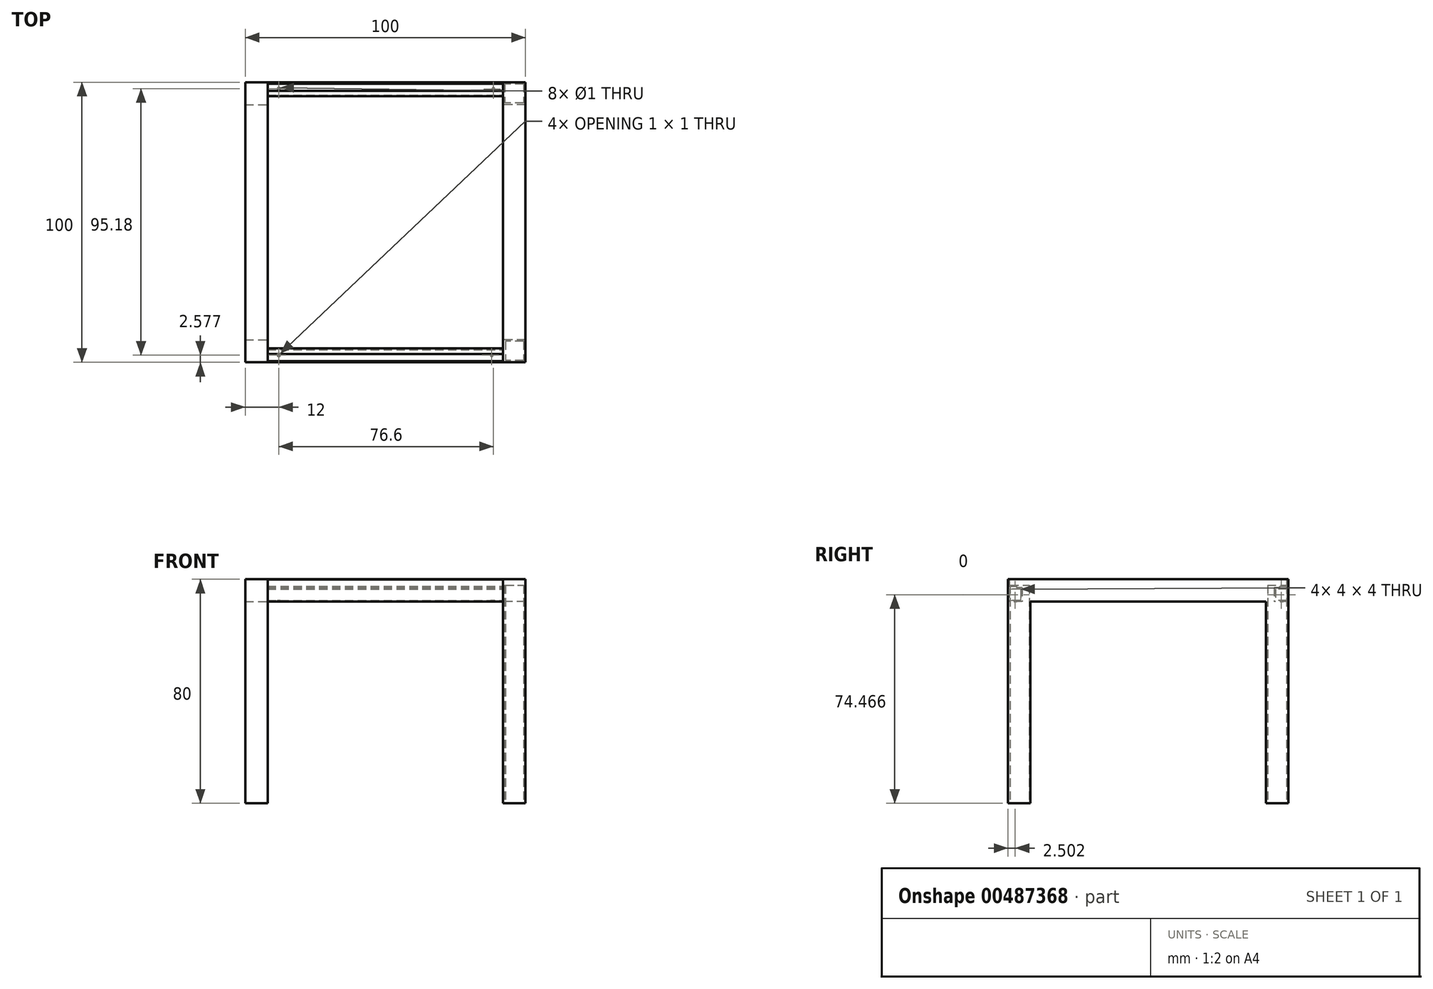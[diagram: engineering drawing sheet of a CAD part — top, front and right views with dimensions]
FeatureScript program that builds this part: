
annotation { "Feature Type Name" : "Feature", "Feature Type Description" : "" }
export const myFeature = defineFeature(function(context is Context, id is Id, definition is map)
    precondition{}
    {
        {
            var Q0;
            Q0=qCreatedBy(makeId("Right.planeOp"),FACE);
            var sketch = newSketch(context, id + "F0", { "sketchPlane" : qUnion([Q0])});
            skLineSegment(sketch, "E0", {"start": v(-60.79, -34.5) * mm, "end": v(-52.79, -34.5) * mm});
            skLineSegment(sketch, "E1", {"start": v(-52.79, -34.5) * mm, "end": v(-52.79, 37.5) * mm});
            skLineSegment(sketch, "E2", {"start": v(-52.79, 37.5) * mm, "end": v(31.21, 37.5) * mm});
            skLineSegment(sketch, "E3", {"start": v(31.21, 37.5) * mm, "end": v(31.21, -34.5) * mm});
            skLineSegment(sketch, "E4", {"start": v(31.21, -34.5) * mm, "end": v(39.21, -34.5) * mm});
            skLineSegment(sketch, "E5", {"start": v(39.21, -34.5) * mm, "end": v(39.21, 45.5) * mm});
            skLineSegment(sketch, "E6", {"start": v(39.21, 45.5) * mm, "end": v(-60.79, 45.5) * mm});
            skLineSegment(sketch, "E7", {"start": v(-60.79, 45.5) * mm, "end": v(-60.79, -34.5) * mm});
            skSolve(sketch);
        }
        {
            var Q0;
            Q0 = qSketchRegion(id + "F0", true);
            extrude(context, id + "F1", {"entities" : qUnion([Q0]), "depth" : 8 * mm});
        }
        {
            var Q0;
            Q0=qCreatedBy(makeId("Top.planeOp"),FACE);
            var sketch = newSketch(context, id + "F2", { "sketchPlane" : qUnion([Q0])});
            skLineSegment(sketch, "E8.bottom", {"start": v(0.9, -60.09) * mm, "end": v(7.35, -60.09) * mm});
            skLineSegment(sketch, "E8.top", {"start": v(0.9, -53.29) * mm, "end": v(7.35, -53.29) * mm});
            skLineSegment(sketch, "E8.left", {"start": v(0.9, -60.09) * mm, "end": v(0.9, -53.29) * mm});
            skLineSegment(sketch, "E8.right", {"start": v(7.35, -60.09) * mm, "end": v(7.35, -53.29) * mm});
            skLineSegment(sketch, "E9.bottom", {"start": v(0.6, 31.81) * mm, "end": v(7.35, 31.81) * mm});
            skLineSegment(sketch, "E9.top", {"start": v(0.6, 38.61) * mm, "end": v(7.35, 38.61) * mm});
            skLineSegment(sketch, "E9.left", {"start": v(0.6, 31.81) * mm, "end": v(0.6, 38.61) * mm});
            skLineSegment(sketch, "E9.right", {"start": v(7.35, 31.81) * mm, "end": v(7.35, 38.61) * mm});
            skSolve(sketch);
        }
        {
            var Q0;
            Q0 = qSketchRegion(id + "F2", true);
            extrude(context, id + "F3", {"entities" : qUnion([Q0]), "operationType" : NewBodyOperationType.REMOVE, "endBound" : BoundingType.SYMMETRIC, "depth" : 86.8 * mm});
        }
        {
            var Q0;
            Q0=qCreatedBy(makeId("Right.planeOp"),FACE);
            var sketch = newSketch(context, id + "F4", { "sketchPlane" : qUnion([Q0])});
            skLineSegment(sketch, "E10.bottom", {"start": v(39.2, 42.5) * mm, "end": v(34.2, 42.5) * mm});
            skLineSegment(sketch, "E10.top", {"start": v(39.2, 37.5) * mm, "end": v(34.2, 37.5) * mm});
            skLineSegment(sketch, "E10.left", {"start": v(39.2, 42.5) * mm, "end": v(39.2, 37.5) * mm});
            skLineSegment(sketch, "E10.right", {"start": v(34.2, 42.5) * mm, "end": v(34.2, 37.5) * mm});
            skLineSegment(sketch, "E11", {"start": v(39.21, 45.5) * mm, "end": v(39.2, 42.5) * mm});
            skLineSegment(sketch, "E12", {"start": v(36.2, 42.5) * mm, "end": v(36.2, 43) * mm});
            skLineSegment(sketch, "E13", {"start": v(36.2, 43) * mm, "end": v(38.71, 43) * mm});
            skLineSegment(sketch, "E14", {"start": v(38.71, 43) * mm, "end": v(38.71, 45.5) * mm});
            skLineSegment(sketch, "E15", {"start": v(38.71, 45.5) * mm, "end": v(39.21, 45.5) * mm});
            skLineSegment(sketch, "E16.bottom", {"start": v(38.7, 42) * mm, "end": v(34.7, 42) * mm});
            skLineSegment(sketch, "E16.top", {"start": v(38.7, 38) * mm, "end": v(34.7, 38) * mm});
            skLineSegment(sketch, "E16.left", {"start": v(38.7, 42) * mm, "end": v(38.7, 38) * mm});
            skLineSegment(sketch, "E16.right", {"start": v(34.7, 42) * mm, "end": v(34.7, 38) * mm});
            skLineSegment(sketch, "E17.bottom", {"start": v(-55.79, 42.5) * mm, "end": v(-60.79, 42.5) * mm});
            skLineSegment(sketch, "E17.top", {"start": v(-55.79, 37.5) * mm, "end": v(-60.79, 37.5) * mm});
            skLineSegment(sketch, "E17.left", {"start": v(-55.79, 42.5) * mm, "end": v(-55.79, 37.5) * mm});
            skLineSegment(sketch, "E17.right", {"start": v(-60.79, 42.5) * mm, "end": v(-60.79, 37.5) * mm});
            skLineSegment(sketch, "E18", {"start": v(-60.79, 45.5) * mm, "end": v(-60.29, 45.5) * mm});
            skLineSegment(sketch, "E19", {"start": v(-60.29, 45.5) * mm, "end": v(-60.29, 43) * mm});
            skLineSegment(sketch, "E20", {"start": v(-60.29, 43) * mm, "end": v(-57.79, 43) * mm});
            skLineSegment(sketch, "E21", {"start": v(-57.79, 43) * mm, "end": v(-57.79, 42.5) * mm});
            skLineSegment(sketch, "E22", {"start": v(-60.79, 45.5) * mm, "end": v(-60.79, 42.5) * mm});
            skLineSegment(sketch, "E23.bottom", {"start": v(-56.29, 41.98) * mm, "end": v(-60.29, 41.98) * mm});
            skLineSegment(sketch, "E23.top", {"start": v(-56.29, 37.98) * mm, "end": v(-60.29, 37.98) * mm});
            skLineSegment(sketch, "E23.left", {"start": v(-56.29, 41.98) * mm, "end": v(-56.29, 37.98) * mm});
            skLineSegment(sketch, "E23.right", {"start": v(-60.29, 41.98) * mm, "end": v(-60.29, 37.98) * mm});
            skLineSegment(sketch, "E24", {"start": v(-57.79, 42.5) * mm, "end": v(-60.79, 42.5) * mm});
            skSolve(sketch);
        }
        {
            var Q0;
            Q0 = qSketchRegion(id + "F4", true);
            extrude(context, id + "F5", {"entities" : qUnion([Q0]), "oppositeDirection" : true, "depth" : 84 * mm});
        }
        {
            var Q0;
            Q0 = qSketchRegion(id + "F4", true);
            extrude(context, id + "F6", {"entities" : qUnion([Q0]), "oppositeDirection" : true, "depth" : 84 * mm});
        }
        {
            var Q0;
            Q0=makeQuery(id+"F1.opExtrude","CAP_FACE",FACE,{"disambiguationData":[OSD([sQuery(id+"F0.wireOp",EDGE,"E0"),sQuery(id+"F0.wireOp",EDGE,"E1"),sQuery(id+"F0.wireOp",EDGE,"E2"),sQuery(id+"F0.wireOp",EDGE,"E3"),sQuery(id+"F0.wireOp",EDGE,"E4"),sQuery(id+"F0.wireOp",EDGE,"E5"),sQuery(id+"F0.wireOp",EDGE,"E6"),sQuery(id+"F0.wireOp",EDGE,"E7")])],"isStart":true});
            extrude(context, id + "F7", {"entities" : qUnion([Q0]), "depth" : 92 * mm, "hasSecondDirection" : true, "secondDirectionOppositeDirection" : false, "secondDirectionDepth" : 84 * mm});
        }
        {
            var Q0;
            Q0=makeQuery(id+"F5.opExtrude","SWEPT_FACE",FACE,{"disambiguationData":[OSD([sQuery(id+"F4.wireOp",EDGE,"E17.top")])]});
            var sketch = newSketch(context, id + "F8", { "sketchPlane" : qUnion([Q0])});
            skCircle(sketch, "E25", {"center": v(-80, 58.21) * mm, "radius": 0.5 * mm});
            skCircle(sketch, "E26", {"center": v(-4, 58.21) * mm, "radius": 0.5 * mm});
            skCircle(sketch, "E27", {"center": v(-3.4, -36.83) * mm, "radius": 0.5 * mm});
            skCircle(sketch, "E28", {"center": v(-80, -36.97) * mm, "radius": 0.5 * mm});
            skSolve(sketch);
        }
        {
            var Q0;
            Q0 = qSketchRegion(id + "F8", true);
            extrude(context, id + "F9", {"entities" : qUnion([Q0]), "operationType" : NewBodyOperationType.REMOVE, "oppositeDirection" : true, "depth" : 4.1 * mm});
        }
    });
